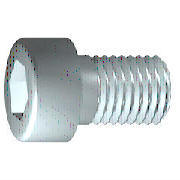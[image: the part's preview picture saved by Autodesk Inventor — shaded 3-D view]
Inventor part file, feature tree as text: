
AUTODESK INVENTOR PART (.ipt)
format: ipt  version: 2018 (Build 220112000, 112)  size: 183,808 bytes
history: native  units: mm (DEFAULTED — no unit token found)
features: sketch x2, extrude x1, plane x1, fillet x1
ambient origin geometry x7: Origin, YZ Plane, XY Plane, X Axis, Y Axis, Z Axis, Center Point
bodies: Solid1 (feature_tree), Body (feature_tree)
feature tree (5):
  extrude  "Slot"  Depth=5.0mm
  plane  "Work Plane1"
  fillet  "Fillet2"  Radius=5.0mm
  sketch  "Sketch1"  dims[d1=22.0mm d2=0.49086mm d3=5.0mm]
  sketch  "Sketch2"  dims[d4=2.5mm d5=60.0deg d6=5.0mm d7=5.0mm d8=4.618802mm d9=8.5mm d10=90.0deg d11=10.0mm d12=0.0mm d13=22.0mm d14=0.0mm d15=0.49076mm d16=0.49076mm d17=0.5mm d19=0.0mm d26=60.0mm d27=45.0deg d28=0.0mm d29=0.0mm d30=0.1mm]
